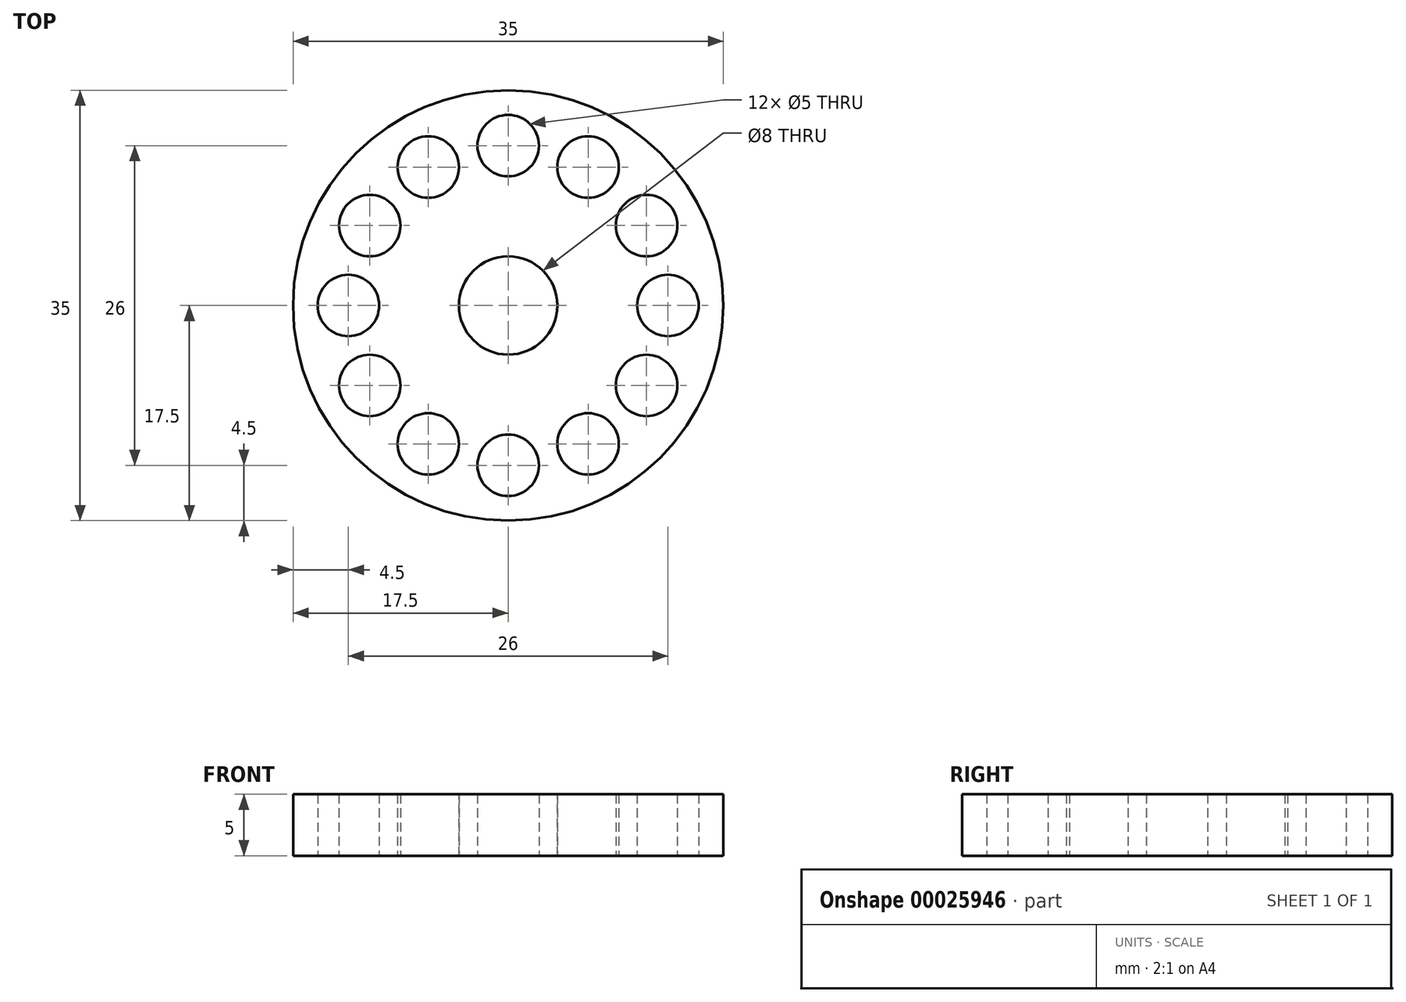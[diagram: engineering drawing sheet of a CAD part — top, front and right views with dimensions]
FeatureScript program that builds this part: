
annotation { "Feature Type Name" : "Feature", "Feature Type Description" : "" }
export const myFeature = defineFeature(function(context is Context, id is Id, definition is map)
    precondition{}
    {
        {
            var Q0;
            Q0=qCreatedBy(makeId("Top.planeOp"),FACE);
            var sketch = newSketch(context, id + "F0", { "sketchPlane" : qUnion([Q0])});
            skCircle(sketch, "E0", {"center": v(0, 0) * mm, "radius": 17.5 * mm});
            skCircle(sketch, "E1", {"center": v(0, 13) * mm, "radius": 2.5 * mm});
            skCircle(sketch, "E2.1.0", {"center": v(-6.5, 11.26) * mm, "radius": 2.5 * mm});
            skCircle(sketch, "E2.2.0", {"center": v(-11.26, 6.5) * mm, "radius": 2.5 * mm});
            skCircle(sketch, "E2.3.0", {"center": v(-13, 0) * mm, "radius": 2.5 * mm});
            skCircle(sketch, "E2.4.0", {"center": v(-11.26, -6.5) * mm, "radius": 2.5 * mm});
            skCircle(sketch, "E2.5.0", {"center": v(-6.5, -11.26) * mm, "radius": 2.5 * mm});
            skCircle(sketch, "E2.6.0", {"center": v(0, -13) * mm, "radius": 2.5 * mm});
            skCircle(sketch, "E2.7.0", {"center": v(6.5, -11.26) * mm, "radius": 2.5 * mm});
            skCircle(sketch, "E2.8.0", {"center": v(11.26, -6.5) * mm, "radius": 2.5 * mm});
            skCircle(sketch, "E2.9.0", {"center": v(13, 0) * mm, "radius": 2.5 * mm});
            skCircle(sketch, "E2.10.0", {"center": v(11.26, 6.5) * mm, "radius": 2.5 * mm});
            skCircle(sketch, "E2.11.0", {"center": v(6.5, 11.26) * mm, "radius": 2.5 * mm});
            skSolve(sketch);
        }
        {
            var Q0;
            Q0=makeQuery(id+"F0.imprint","IMPRINT",FACE,{"disambiguationData":[TD([[makeQuery(id+"F0.imprint","IMPRINT",EDGE,{"derivedFrom":sQuery(id+"F0.wireOp",EDGE,"E0")}),1.0]])]});
            extrude(context, id + "F1", {"entities" : qUnion([Q0]), "depth" : 5 * mm, "symmetric" : true});
        }
        {
            var Q0;
            Q0=makeQuery(id+"F1.opExtrude","CAP_FACE",FACE,{"disambiguationData":[OSD([sQuery(id+"F0.wireOp",EDGE,"E0"),sQuery(id+"F0.wireOp",EDGE,"E1"),sQuery(id+"F0.wireOp",EDGE,"E2.1.0"),sQuery(id+"F0.wireOp",EDGE,"E2.2.0"),sQuery(id+"F0.wireOp",EDGE,"E2.3.0"),sQuery(id+"F0.wireOp",EDGE,"E2.4.0"),sQuery(id+"F0.wireOp",EDGE,"E2.5.0"),sQuery(id+"F0.wireOp",EDGE,"E2.6.0"),sQuery(id+"F0.wireOp",EDGE,"E2.7.0"),sQuery(id+"F0.wireOp",EDGE,"E2.8.0"),sQuery(id+"F0.wireOp",EDGE,"E2.9.0"),sQuery(id+"F0.wireOp",EDGE,"E2.10.0"),sQuery(id+"F0.wireOp",EDGE,"E2.11.0")])],"isStart":false});
            var sketch = newSketch(context, id + "F2", { "sketchPlane" : qUnion([Q0])});
            skCircle(sketch, "E3", {"center": v(0, 0) * mm, "radius": 4 * mm});
            skSolve(sketch);
        }
        {
            var Q0;
            Q0=makeQuery(id+"F2.imprint","IMPRINT",FACE,{"disambiguationData":[TD([[makeQuery(id+"F2.imprint","IMPRINT",EDGE,{"derivedFrom":sQuery(id+"F2.wireOp",EDGE,"E3")}),1.0]])]});
            extrude(context, id + "F3", {"entities" : qUnion([Q0]), "operationType" : NewBodyOperationType.REMOVE, "endBound" : BoundingType.UP_TO_NEXT, "oppositeDirection" : true, "depth" : 25 * mm});
        }
    });
